# Revit family: Shower-Shower_Trim-KOHLER-Pinstripe-K-TS13134
name_source: partatom
category: Plumbing Fixtures
revit_build: Autodesk Revit 2015 (Build: 20140606_1530(x64)
units: mm (PartAtom-declared; Revit-internal decimal feet)

## types (12) — shared parameters
ADA Compliant = No
Assembly Code = D2010700
CW Connection = No
Cold Water Inlet = Cold Water Inlet
Date Modified = 04/09/2019
Default Elevation = 42"
Drain Included = No
Flow Rate = 3 GPM
HW Connection = Yes
Handle Height = 5 1/8"
Height = 6 15/16"
Hot Water Inlet = Tempered Water Inlet
Length = 11 1/4"
Manufacturer = KOHLER Co.
MasterFormat 1995 = 15410
MasterFormat 2004 = 22.41.23
Material = Premium Metal Construction
Pressure = 80.00 psi
Product Documentation Link = https://www.us.kohler.com
Product Name = Pinstripe
Product Page URL = http://www.us.kohler.com
URL = https://www.us.kohler.com
Vent Connection = No
Waste Connection = No
Waste Water Outlet = Waste Water Outlet
WaterSense Certified = No
Width = 6 11/16"

## per-type parameters (varying)
| type | 3A | 3B | 4A | 4B | Description | Distance1 | Finish | Handle Clearance | Model | Type | Visibility | Visibility 1 |
| Pure Rite-Temp Shower, Cross-Handle, CP-Polished Chrome | Yes | No | No | No | Pure Rite-Temp shower valve trim with cross handle and 2.5 gpm showerhead | 1 5/8" | Kohler-Metal-CP-Polished_Chrome | 3 1/4" | K-TS13134-3A-CP | 1 | Yes | No |
| Pure Rite-Temp Shower, Cross-Handle, SN-Vibrant Polished Nickel | Yes | No | No | No | Pure Rite-Temp shower valve trim with cross handle and 2.5 gpm showerhead | 1 5/8" | Kohler-Metal-SN-Vibrant_Polished_Nickel | 3 1/4" | K-TS13134-3A-SN | 2 | Yes | No |
| Pure Rite-Temp Shower, Cross-Handle, BN-Vibrant Brushed Nickel | Yes | No | No | No | Pure Rite-Temp shower valve trim with cross handle and 2.5 gpm showerhead | 1 5/8" | Kohler-Metal-BN-Vibrant_Brushed_Nickel | 3 1/4" | K-TS13134-3A-BN | 3 | Yes | No |
| Rite-Temp Shower, Cross-Handle, CP-Polished Chrome | No | Yes | No | No | Rite-Temp shower valve trim with cross handle and 2.5 gpm showerhead | 1 5/8" | Kohler-Metal-CP-Polished_Chrome | 3 1/4" | K-TS13134-3B-CP | 4 | Yes | No |
| Rite-Temp Shower, Cross-Handle, SN-Vibrant Polished Nickel | No | Yes | No | No | Rite-Temp shower valve trim with cross handle and 2.5 gpm showerhead | 1 5/8" | Kohler-Metal-SN-Vibrant_Polished_Nickel | 3 1/4" | K-TS13134-3B-SN | 5 | Yes | No |
| Rite-Temp Shower, Cross-Handle, BN-Vibrant Brushed Nickel | No | Yes | No | No | Rite-Temp shower valve trim with cross handle and 2.5 gpm showerhead | 1 5/8" | Kohler-Metal-BN-Vibrant_Brushed_Nickel | 3 1/4" | K-TS13134-3B-BN | 6 | Yes | No |
| Pure Rite-Temp Shower, Lever-Handle, CP-Polished Chrome | No | No | Yes | No | Pure Rite-Temp shower valve trim with lever handle and 2.5 gpm showerhead | 0" | Kohler-Metal-CP-Polished_Chrome | 3" | K-TS13134-4A-CP | 7 | No | Yes |
| Pure Rite-Temp Shower, Lever-Handle, SN-Vibrant Polished Nickel | No | No | Yes | No | Pure Rite-Temp shower valve trim with lever handle and 2.5 gpm showerhead | 0" | Kohler-Metal-SN-Vibrant_Polished_Nickel | 3" | K-TS13134-4A-SN | 8 | No | Yes |
| Pure Rite-Temp Shower, Lever-Handle, BN-Vibrant Brushed Nickel | No | No | Yes | No | Pure Rite-Temp shower valve trim with lever handle and 2.5 gpm showerhead | 0" | Kohler-Metal-BN-Vibrant_Brushed_Nickel | 3" | K-TS13134-4A-BN | 9 | No | Yes |
| Rite-Temp Shower, Lever-Handle, CP-Polished Chrome | No | No | No | Yes | Rite-Temp shower valve trim with lever handle and 2.5 gpm showerhead | 0" | Kohler-Metal-CP-Polished_Chrome | 3" | K-TS13134-4B-CP | 10 | No | Yes |
| Rite-Temp Shower, Lever-Handle, SN-Vibrant Polished Nickel | No | No | No | Yes | Rite-Temp shower valve trim with lever handle and 2.5 gpm showerhead | 0" | Kohler-Metal-SN-Vibrant_Polished_Nickel | 3" | K-TS13134-4B-SN | 11 | No | Yes |
| Rite-Temp Shower, Lever-Handle, BN-Vibrant Brushed Nickel | No | No | No | Yes | Rite-Temp shower valve trim with lever handle and 2.5 gpm showerhead | 0" | Kohler-Metal-BN-Vibrant_Brushed_Nickel | 3" | K-TS13134-4B-BN | 12 | No | Yes |

## geometry (parser evidence)
native form markers: Sweep x9
no freeform markers — native parametric forms only
